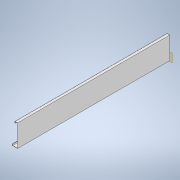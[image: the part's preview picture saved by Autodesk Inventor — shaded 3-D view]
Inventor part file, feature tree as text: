
AUTODESK INVENTOR PART (.ipt)
format: ipt  version: 2020 (Build 240168000, 168)  size: 106,496 bytes
history: native  units: mm
features: other x5, plane x1, extrude x1, sketch x1
ambient origin geometry x8: Origin, YZ Plane, XZ Plane, XY Plane, X Axis, Y Axis, Z Axis, Center Point
bodies: Body1 (feature_tree)
feature tree (8):
  plane  "Work Plane1"
  extrude  "Extrusion2"  Depth=80.0mm
  sketch  "Sketch1"  dims[d2=25.0mm d4=80.0mm d5=25.0mm d6=3.5mm d7=350.0mm d8=2400.0mm d9=0.0mm]
  parser-record x1  (decoder bookkeeping rows leaked as tree rows — omitted from the tree; the rows remain in map.json)
  other  "estufa morango 20.iam"
  other  "corners 20feet:1"
  other  "corners bottom:1"
  other  "corner_BL_MIR:1"
note: 1 file-system path scrubbed to <path> (originals preserved in map.json)
